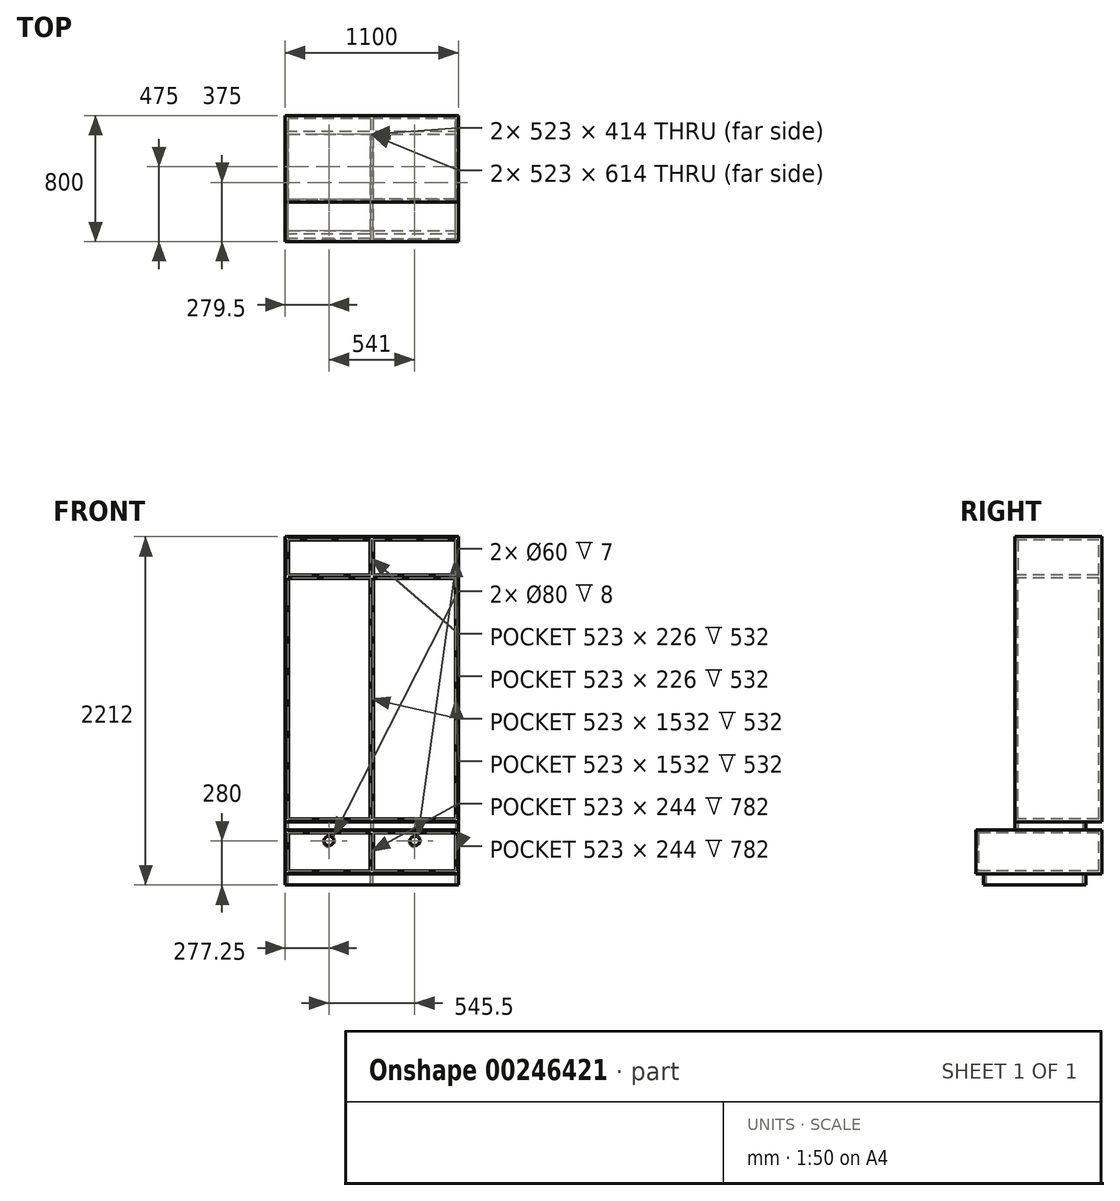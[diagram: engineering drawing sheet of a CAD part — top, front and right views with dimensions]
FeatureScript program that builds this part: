
annotation { "Feature Type Name" : "Feature", "Feature Type Description" : "" }
export const myFeature = defineFeature(function(context is Context, id is Id, definition is map)
    precondition{}
    {
        {
            var Q0;
            Q0=qCreatedBy(makeId("Top.planeOp"),FACE);
            var sketch = newSketch(context, id + "F0", { "sketchPlane" : qUnion([Q0])});
            skLineSegment(sketch, "E0.bottom", {"start": v(0, 0) * mm, "end": v(-1100, 0) * mm});
            skLineSegment(sketch, "E0.top", {"start": v(0, 800) * mm, "end": v(-1100, 800) * mm});
            skLineSegment(sketch, "E0.left", {"start": v(0, 0) * mm, "end": v(0, 800) * mm});
            skLineSegment(sketch, "E0.right", {"start": v(-1100, 0) * mm, "end": v(-1100, 800) * mm});
            skSolve(sketch);
        }
        {
            var Q0;
            Q0=makeQuery(id+"F0.imprint","IMPRINT",FACE,{"disambiguationData":[TD([[makeQuery(id+"F0.imprint","IMPRINT",EDGE,{"derivedFrom":sQuery(id+"F0.wireOp",EDGE,"E0.bottom")}),-1.0]])]});
            extrude(context, id + "F1", {"entities" : qUnion([Q0]), "depth" : (350 - 70) * mm});
        }
        {
            var Q0;
            Q0=makeQuery(id+"F1.opExtrude","SWEPT_FACE",FACE,{"disambiguationData":[OSD([sQuery(id+"F0.wireOp",EDGE,"E0.bottom")])]});
            shell(context, id + "F2", {"entities" : qUnion([Q0]), "thickness" : 18 * mm});
        }
        {
            var Q0;
            Q0=makeQuery(id+"F1.opExtrude","SWEPT_FACE",FACE,{"disambiguationData":[OSD([sQuery(id+"F0.wireOp",EDGE,"E0.bottom")])]});
            var sketch = newSketch(context, id + "F3", { "sketchPlane" : qUnion([Q0])});
            skLineSegment(sketch, "E1.bottom", {"start": v(-559, 262) * mm, "end": v(-541, 262) * mm});
            skLineSegment(sketch, "E1.top", {"start": v(-559, 18) * mm, "end": v(-541, 18) * mm});
            skLineSegment(sketch, "E1.left", {"start": v(-559, 262) * mm, "end": v(-559, 18) * mm});
            skLineSegment(sketch, "E1.right", {"start": v(-541, 262) * mm, "end": v(-541, 18) * mm});
            skSolve(sketch);
        }
        {
            var Q0;
            Q0=qSketchRegion(id+"F3",true);
            var Q1;
            Q1=makeQuery(id+"F2.opShell","OFFSET_FACE",FACE,{"disambiguationData":[OSD([sQuery(id+"F0.wireOp",EDGE,"E0.top")])]});
            extrude(context, id + "F4", {"entities" : qUnion([Q0]), "operationType" : NewBodyOperationType.ADD, "endBound" : BoundingType.UP_TO_SURFACE, "oppositeDirection" : true, "endBoundEntityFace" : qUnion([Q1]), "depth" : 25 * mm});
        }
        {
            var Q0;
            Q0=makeQuery(id+"F4.boolean.opBoolean","MERGE",FACE,{"derivedFrom":[makeQuery(id+"F1.opExtrude","SWEPT_FACE",FACE,{"disambiguationData":[OSD([sQuery(id+"F0.wireOp",EDGE,"E0.bottom")])]}),makeQuery(id+"F4.opExtrude","CAP_FACE",FACE,{"disambiguationData":[OSD([sQuery(id+"F3.wireOp",EDGE,"E1.bottom"),sQuery(id+"F3.wireOp",EDGE,"E1.top"),sQuery(id+"F3.wireOp",EDGE,"E1.left"),sQuery(id+"F3.wireOp",EDGE,"E1.right")])],"isStart":true})]});
            var sketch = newSketch(context, id + "F5", { "sketchPlane" : qUnion([Q0])});
            skLineSegment(sketch, "E2.0", {"start": v(-561, 260) * mm, "end": v(-1080, 260) * mm});
            skLineSegment(sketch, "E2.1", {"start": v(-561, 260) * mm, "end": v(-561, 20) * mm});
            skLineSegment(sketch, "E2.2", {"start": v(-561, 20) * mm, "end": v(-1080, 20) * mm});
            skLineSegment(sketch, "E2.3", {"start": v(-1080, 260) * mm, "end": v(-1080, 20) * mm});
            skSolve(sketch);
        }
        {
            var Q0;
            Q0=qSketchRegion(id+"F5",true);
            extrude(context, id + "F6", {"entities" : qUnion([Q0]), "oppositeDirection" : true, "depth" : 18 * mm});
        }
        {
            var Q0;
            Q0=makeQuery(id+"F1.opExtrude","SWEPT_FACE",FACE,{"disambiguationData":[OSD([sQuery(id+"F0.wireOp",EDGE,"E0.left")])]});
            cPlane(context, id + "F7", {"entities" : qUnion([Q0]), "cplaneType" : CPlaneType.OFFSET, "offset" : (1100 / 2) * mm, "oppositeDirection" : true, "width" : 150 * mm, "height" : 150 * mm});
        }
        {
            var Q0;
            Q0=makeQuery(id+"F6.opExtrude","CAP_FACE",FACE,{"disambiguationData":[OSD([sQuery(id+"F5.wireOp",EDGE,"E2.0"),sQuery(id+"F5.wireOp",EDGE,"E2.1"),sQuery(id+"F5.wireOp",EDGE,"E2.2"),sQuery(id+"F5.wireOp",EDGE,"E2.3")])],"isStart":true});
            var sketch = newSketch(context, id + "F8", { "sketchPlane" : qUnion([Q0])});
            skCircle(sketch, "E3", {"center": v(-822.75, 210) * mm, "radius": 30 * mm});
            skSolve(sketch);
        }
        {
            var Q0;
            Q0=qSketchRegion(id+"F8",true);
            extrude(context, id + "F9", {"entities" : qUnion([Q0]), "operationType" : NewBodyOperationType.REMOVE, "oppositeDirection" : true, "depth" : 15 * mm});
        }
        {
            var Q0;
            Q0=makeQuery(id+"F9.boolean.opBoolean","COPY",FACE,{"derivedFrom":makeQuery(id+"F9.opExtrude","CAP_FACE",FACE,{"disambiguationData":[OSD([sQuery(id+"F8.wireOp",EDGE,"E3")])],"isStart":false})});
            var sketch = newSketch(context, id + "F10", { "sketchPlane" : qUnion([Q0])});
            skCircle(sketch, "E4.0", {"center": v(-822.75, 210) * mm, "radius": 40 * mm});
            skSolve(sketch);
        }
        {
            var Q0;
            Q0=qSketchRegion(id+"F10",true);
            extrude(context, id + "F11", {"entities" : qUnion([Q0]), "operationType" : NewBodyOperationType.REMOVE, "depth" : 8 * mm});
        }
        {
            var Q0;
            Q0=makeQuery(id+"F6.opExtrude","SWEPT_BODY",BODY,{"disambiguationData":[OSD([sQuery(id+"F5.wireOp",EDGE,"E2.0"),sQuery(id+"F5.wireOp",EDGE,"E2.1"),sQuery(id+"F5.wireOp",EDGE,"E2.2"),sQuery(id+"F5.wireOp",EDGE,"E2.3")])]});
            var Q1;
            Q1=qCreatedBy(id+"F7.planeOp",FACE);
            mirror(context, id + "F12", {"entities" : qUnion([Q0]), "mirrorPlane" : qUnion([Q1])});
        }
        {
            var Q0;
            Q0=makeQuery(id+"F1.opExtrude","CAP_FACE",FACE,{"disambiguationData":[OSD([sQuery(id+"F0.wireOp",EDGE,"E0.bottom"),sQuery(id+"F0.wireOp",EDGE,"E0.top"),sQuery(id+"F0.wireOp",EDGE,"E0.left"),sQuery(id+"F0.wireOp",EDGE,"E0.right")])],"isStart":true});
            var sketch = newSketch(context, id + "F13", { "sketchPlane" : qUnion([Q0])});
            skLineSegment(sketch, "E5.bottom", {"start": v(-1100, -50) * mm, "end": v(0, -50) * mm});
            skLineSegment(sketch, "E5.top", {"start": v(-1100, -700) * mm, "end": v(0, -700) * mm});
            skLineSegment(sketch, "E5.left", {"start": v(-1100, -50) * mm, "end": v(-1100, -700) * mm});
            skLineSegment(sketch, "E5.right", {"start": v(0, -50) * mm, "end": v(0, -700) * mm});
            skLineSegment(sketch, "E6.0", {"start": v(-1082, -68) * mm, "end": v(-559, -68) * mm});
            skLineSegment(sketch, "E6.1", {"start": v(-1082, -68) * mm, "end": v(-1082, -682) * mm});
            skLineSegment(sketch, "E6.2", {"start": v(-1082, -682) * mm, "end": v(-559, -682) * mm});
            skLineSegment(sketch, "E6.3", {"start": v(-18, -68) * mm, "end": v(-18, -682) * mm});
            skLineSegment(sketch, "E7.left", {"start": v(-559, -68) * mm, "end": v(-559, -682) * mm});
            skLineSegment(sketch, "E7.right", {"start": v(-541, -68) * mm, "end": v(-541, -682) * mm});
            skLineSegment(sketch, "E8.trimOffspring", {"start": v(-541, -68) * mm, "end": v(-18, -68) * mm});
            skLineSegment(sketch, "E9.trimOffspring", {"start": v(-541, -682) * mm, "end": v(-18, -682) * mm});
            skSolve(sketch);
        }
        {
            var Q0;
            Q0=qSketchRegion(id+"F13",true);
            extrude(context, id + "F14", {"entities" : qUnion([Q0]), "depth" : 70 * mm});
        }
        {
            var Q0;
            Q0=makeQuery(id+"F1.opExtrude","CAP_FACE",FACE,{"disambiguationData":[OSD([sQuery(id+"F0.wireOp",EDGE,"E0.bottom"),sQuery(id+"F0.wireOp",EDGE,"E0.top"),sQuery(id+"F0.wireOp",EDGE,"E0.left"),sQuery(id+"F0.wireOp",EDGE,"E0.right")])],"isStart":false});
            var sketch = newSketch(context, id + "F15", { "sketchPlane" : qUnion([Q0])});
            skLineSegment(sketch, "E10.bottom", {"start": v(-1100, 700) * mm, "end": v(0, 700) * mm});
            skLineSegment(sketch, "E10.top", {"start": v(-1100, 250) * mm, "end": v(0, 250) * mm});
            skLineSegment(sketch, "E10.left", {"start": v(-1100, 700) * mm, "end": v(-1100, 250) * mm});
            skLineSegment(sketch, "E10.right", {"start": v(0, 700) * mm, "end": v(0, 250) * mm});
            skLineSegment(sketch, "E11.0", {"start": v(-1082, 682) * mm, "end": v(-559, 682) * mm});
            skLineSegment(sketch, "E11.1", {"start": v(-1082, 682) * mm, "end": v(-1082, 268) * mm});
            skLineSegment(sketch, "E11.2", {"start": v(-1082, 268) * mm, "end": v(-559, 268) * mm});
            skLineSegment(sketch, "E11.3", {"start": v(-18, 682) * mm, "end": v(-18, 268) * mm});
            skLineSegment(sketch, "E12.left", {"start": v(-559, 682) * mm, "end": v(-559, 268) * mm});
            skLineSegment(sketch, "E12.right", {"start": v(-541, 682) * mm, "end": v(-541, 268) * mm});
            skLineSegment(sketch, "E13.trimOffspring", {"start": v(-541, 682) * mm, "end": v(-18, 682) * mm});
            skLineSegment(sketch, "E14.trimOffspring", {"start": v(-541, 268) * mm, "end": v(-18, 268) * mm});
            skSolve(sketch);
        }
        {
            var Q0;
            Q0=qSketchRegion(id+"F15",true);
            extrude(context, id + "F16", {"entities" : qUnion([Q0]), "depth" : 50 * mm});
        }
        {
            var Q0;
            Q0=makeQuery(id+"F16.opExtrude","CAP_FACE",FACE,{"disambiguationData":[OSD([sQuery(id+"F15.wireOp",EDGE,"E10.bottom"),sQuery(id+"F15.wireOp",EDGE,"E10.top"),sQuery(id+"F15.wireOp",EDGE,"E10.left"),sQuery(id+"F15.wireOp",EDGE,"E10.right"),sQuery(id+"F15.wireOp",EDGE,"E11.0"),sQuery(id+"F15.wireOp",EDGE,"E11.1"),sQuery(id+"F15.wireOp",EDGE,"E11.2"),sQuery(id+"F15.wireOp",EDGE,"E11.3"),sQuery(id+"F15.wireOp",EDGE,"E12.left"),sQuery(id+"F15.wireOp",EDGE,"E12.right"),sQuery(id+"F15.wireOp",EDGE,"E13.trimOffspring"),sQuery(id+"F15.wireOp",EDGE,"E14.trimOffspring")])],"isStart":false});
            var sketch = newSketch(context, id + "F17", { "sketchPlane" : qUnion([Q0])});
            skLineSegment(sketch, "E15.bottom", {"start": v(-1100, 250) * mm, "end": v(0, 250) * mm});
            skLineSegment(sketch, "E15.top", {"start": v(-1100, 800) * mm, "end": v(0, 800) * mm});
            skLineSegment(sketch, "E15.left", {"start": v(-1100, 250) * mm, "end": v(-1100, 800) * mm});
            skLineSegment(sketch, "E15.right", {"start": v(0, 250) * mm, "end": v(0, 800) * mm});
            skSolve(sketch);
        }
        {
            var Q0;
            Q0=qSketchRegion(id+"F17",true);
            extrude(context, id + "F18", {"entities" : qUnion([Q0]), "depth" : (2230 - 350 - 50 - 18) * mm});
        }
        {
            var Q0;
            Q0=makeQuery(id+"F18.opExtrude","SWEPT_FACE",FACE,{"disambiguationData":[OSD([sQuery(id+"F17.wireOp",EDGE,"E15.bottom")])]});
            shell(context, id + "F19", {"entities" : qUnion([Q0]), "thickness" : 18 * mm});
        }
        {
            var Q0;
            Q0=makeQuery(id+"F18.opExtrude","SWEPT_FACE",FACE,{"disambiguationData":[OSD([sQuery(id+"F17.wireOp",EDGE,"E15.bottom")])]});
            var sketch = newSketch(context, id + "F20", { "sketchPlane" : qUnion([Q0])});
            skLineSegment(sketch, "E16.bottom", {"start": v(-559, 348) * mm, "end": v(-541, 348) * mm});
            skLineSegment(sketch, "E16.top", {"start": v(-559, 2124) * mm, "end": v(-541, 2124) * mm});
            skLineSegment(sketch, "E16.left", {"start": v(-559, 348) * mm, "end": v(-559, 2124) * mm});
            skLineSegment(sketch, "E16.right", {"start": v(-541, 348) * mm, "end": v(-541, 2124) * mm});
            skLineSegment(sketch, "E17.bottom", {"start": v(-18, 1898) * mm, "end": v(-1082, 1898) * mm});
            skLineSegment(sketch, "E17.top", {"start": v(-18, 1880) * mm, "end": v(-1082, 1880) * mm});
            skLineSegment(sketch, "E17.left", {"start": v(-18, 1898) * mm, "end": v(-18, 1880) * mm});
            skLineSegment(sketch, "E17.right", {"start": v(-1082, 1898) * mm, "end": v(-1082, 1880) * mm});
            skSolve(sketch);
        }
        {
            var Q0;
            Q0=qSketchRegion(id+"F20",true);
            extrude(context, id + "F21", {"entities" : qUnion([Q0]), "operationType" : NewBodyOperationType.ADD, "endBound" : BoundingType.UP_TO_NEXT, "oppositeDirection" : true, "depth" : 25 * mm});
        }
        {
            var Q0;
            Q0=makeQuery(id+"F21.boolean.opBoolean","MERGE",FACE,{"derivedFrom":[makeQuery(id+"F18.opExtrude","SWEPT_FACE",FACE,{"disambiguationData":[OSD([sQuery(id+"F17.wireOp",EDGE,"E15.bottom")])]}),makeQuery(id+"F21.opExtrude","CAP_FACE",FACE,{"disambiguationData":[OSD([sQuery(id+"F20.wireOp",EDGE,"E16.bottom"),sQuery(id+"F20.wireOp",EDGE,"E16.top"),sQuery(id+"F20.wireOp",EDGE,"E16.left"),sQuery(id+"F20.wireOp",EDGE,"E16.right"),sQuery(id+"F20.wireOp",EDGE,"E17.bottom"),sQuery(id+"F20.wireOp",EDGE,"E17.top"),sQuery(id+"F20.wireOp",EDGE,"E17.left"),sQuery(id+"F20.wireOp",EDGE,"E17.right")])],"isStart":true})]});
            var sketch = newSketch(context, id + "F22", { "sketchPlane" : qUnion([Q0])});
            skLineSegment(sketch, "E18.0", {"start": v(-1080, 350) * mm, "end": v(-561, 350) * mm});
            skLineSegment(sketch, "E18.1", {"start": v(-1080, 1878) * mm, "end": v(-1080, 350) * mm});
            skLineSegment(sketch, "E18.2", {"start": v(-561, 1878) * mm, "end": v(-1080, 1878) * mm});
            skLineSegment(sketch, "E18.3", {"start": v(-561, 350) * mm, "end": v(-561, 1878) * mm});
            skLineSegment(sketch, "E19.0", {"start": v(-1080, 1900) * mm, "end": v(-561, 1900) * mm});
            skLineSegment(sketch, "E19.1", {"start": v(-1080, 2122) * mm, "end": v(-1080, 1900) * mm});
            skLineSegment(sketch, "E19.2", {"start": v(-561, 2122) * mm, "end": v(-1080, 2122) * mm});
            skLineSegment(sketch, "E19.3", {"start": v(-561, 1900) * mm, "end": v(-561, 2122) * mm});
            skLineSegment(sketch, "E20.0", {"start": v(-539, 2122) * mm, "end": v(-539, 1900) * mm});
            skLineSegment(sketch, "E20.1", {"start": v(-20, 2122) * mm, "end": v(-539, 2122) * mm});
            skLineSegment(sketch, "E20.2", {"start": v(-20, 1900) * mm, "end": v(-20, 2122) * mm});
            skLineSegment(sketch, "E20.3", {"start": v(-539, 1900) * mm, "end": v(-20, 1900) * mm});
            skLineSegment(sketch, "E21.0", {"start": v(-20, 350) * mm, "end": v(-20, 1878) * mm});
            skLineSegment(sketch, "E21.1", {"start": v(-539, 350) * mm, "end": v(-20, 350) * mm});
            skLineSegment(sketch, "E21.2", {"start": v(-539, 1878) * mm, "end": v(-539, 350) * mm});
            skLineSegment(sketch, "E21.3", {"start": v(-20, 1878) * mm, "end": v(-539, 1878) * mm});
            skSolve(sketch);
        }
        {
            var Q0;
            Q0=qSketchRegion(id+"F22",true);
            extrude(context, id + "F23", {"entities" : qUnion([Q0]), "oppositeDirection" : true, "depth" : 18 * mm});
        }
    });
